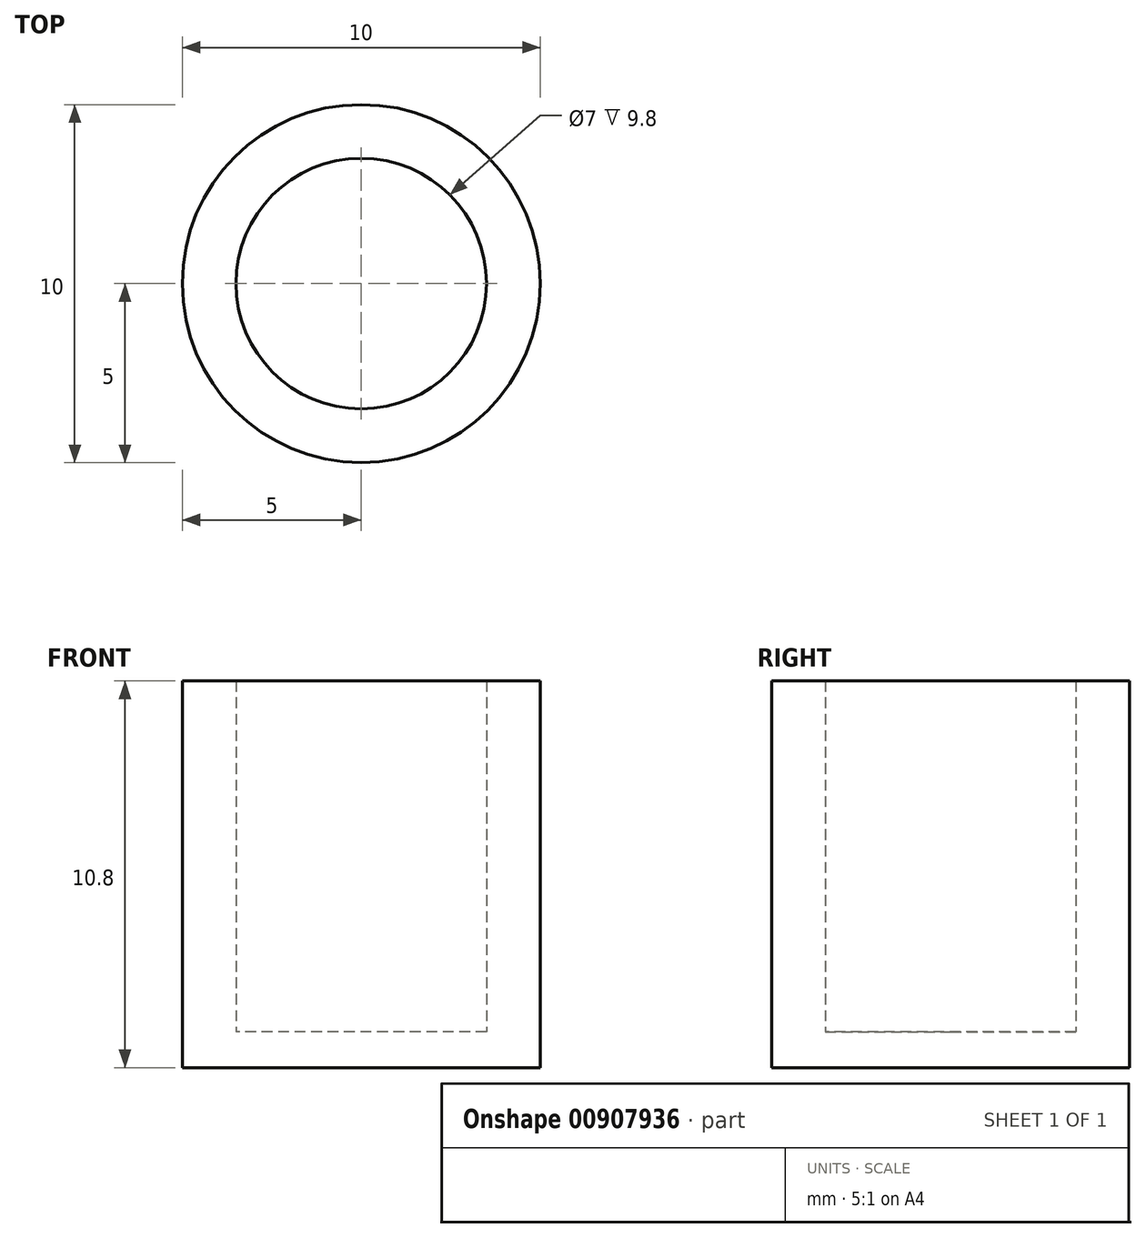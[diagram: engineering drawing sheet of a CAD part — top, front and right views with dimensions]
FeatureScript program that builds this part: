
annotation { "Feature Type Name" : "Feature", "Feature Type Description" : "" }
export const myFeature = defineFeature(function(context is Context, id is Id, definition is map)
    precondition{}
    {
        {
            var Q0;
            Q0=qCreatedBy(makeId("Top.planeOp"),FACE);
            var sketch = newSketch(context, id + "F0", { "sketchPlane" : qUnion([Q0])});
            skCircle(sketch, "E0", {"center": v(0, 0) * mm, "radius": 5 * mm});
            skSolve(sketch);
        }
        {
            var Q0;
            Q0=makeQuery(id+"F0.imprint","IMPRINT",FACE,{"disambiguationData":[TD([[makeQuery(id+"F0.imprint","IMPRINT",EDGE,{"derivedFrom":sQuery(id+"F0.wireOp",EDGE,"E0")}),1.0]])]});
            extrude(context, id + "F1", {"entities" : qUnion([Q0]), "depth" : 1 * mm, "offsetDistance" : 25.4 * mm});
        }
        {
            var Q0;
            Q0=makeQuery(id+"F1.opExtrude","CAP_FACE",FACE,{"disambiguationData":[OSD([sQuery(id+"F0.wireOp",EDGE,"E0")])],"isStart":false});
            var sketch = newSketch(context, id + "F2", { "sketchPlane" : qUnion([Q0])});
            skCircle(sketch, "E1", {"center": v(0, 0) * mm, "radius": 5 * mm});
            skCircle(sketch, "E2", {"center": v(0, 0) * mm, "radius": 3.5 * mm});
            skSolve(sketch);
        }
        {
            var Q0;
            Q0=makeQuery(id+"F2.imprint","IMPRINT",FACE,{"disambiguationData":[TD([[makeQuery(id+"F2.imprint","IMPRINT",EDGE,{"derivedFrom":sQuery(id+"F2.wireOp",EDGE,"E2")}),-1.0]])]});
            extrude(context, id + "F3", {"entities" : qUnion([Q0]), "operationType" : NewBodyOperationType.ADD, "depth" : 9.8 * mm, "offsetDistance" : 25.4 * mm});
        }
        {
            var Q0;
            Q0=makeQuery(id+"F1.opExtrude","CAP_FACE",FACE,{"disambiguationData":[OSD([sQuery(id+"F0.wireOp",EDGE,"E0")])],"isStart":false});
            var sketch = newSketch(context, id + "F4", { "sketchPlane" : qUnion([Q0])});
            skArc(sketch, "E3", {"start": v(0, 2) * mm, "mid": v(-2, 0) * mm, "end": v(0, -2) * mm});
            skSolve(sketch);
        }
        {
            var Q0;
            Q0=sQuery(id+"F4.wireOp",EDGE,"E3");
            extrude(context, id + "F5", {"bodyType" : ToolBodyType.SURFACE, "surfaceEntities" : qUnion([Q0]), "depth" : 7.5 * mm, "offsetDistance" : 25.4 * mm});
        }
    });
